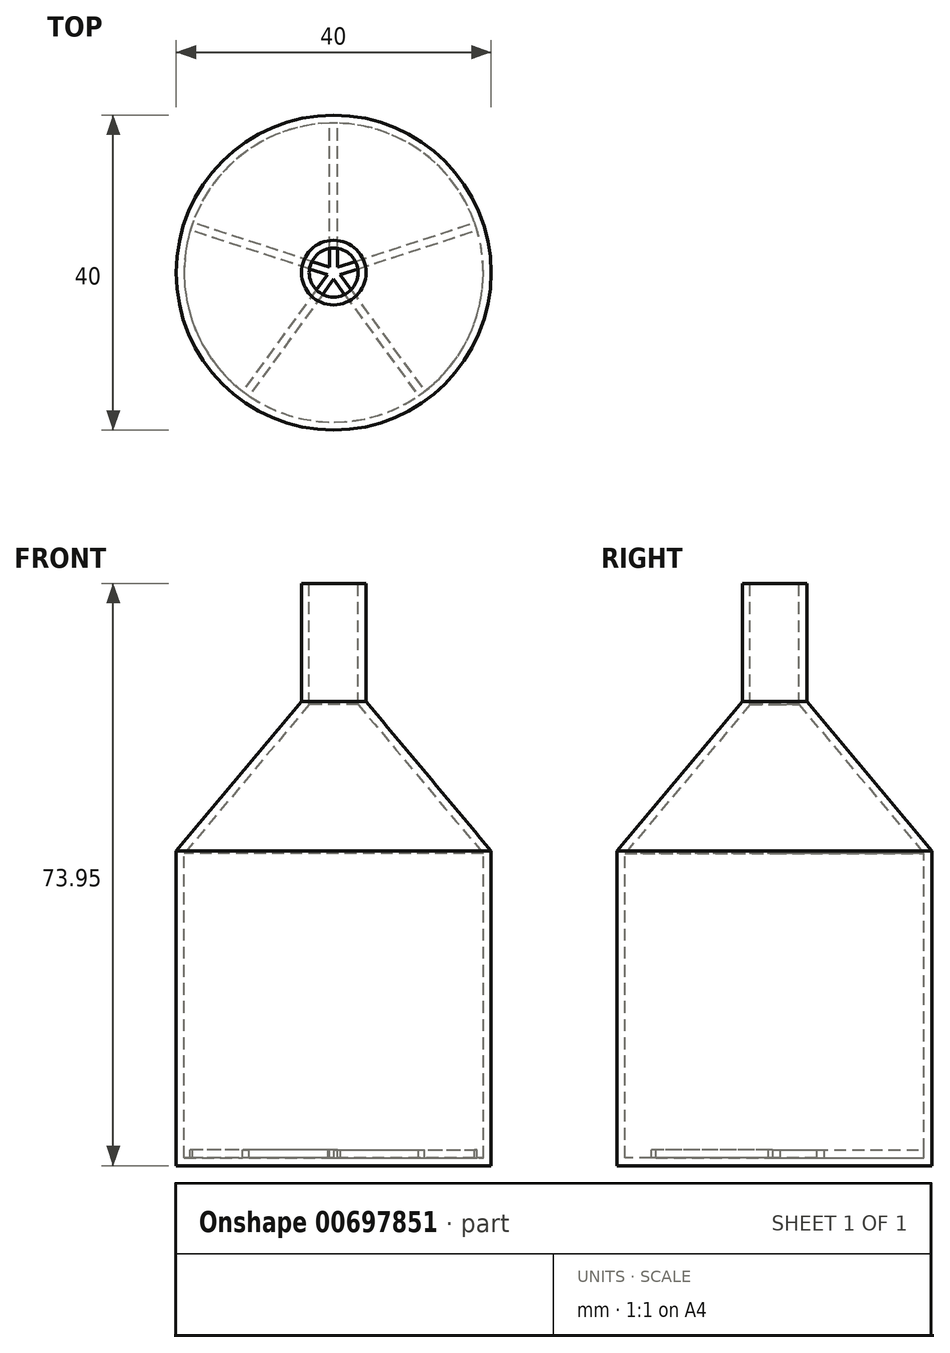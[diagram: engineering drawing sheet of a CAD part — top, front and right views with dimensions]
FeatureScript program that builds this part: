
annotation { "Feature Type Name" : "Feature", "Feature Type Description" : "" }
export const myFeature = defineFeature(function(context is Context, id is Id, definition is map)
    precondition{}
    {
        {
            var Q0;
            Q0=qCreatedBy(makeId("Front.planeOp"),FACE);
            var sketch = newSketch(context, id + "F0", { "sketchPlane" : qUnion([Q0])});
            skLineSegment(sketch, "E0", {"start": v(0, -1) * mm, "end": v(20, -1) * mm});
            skLineSegment(sketch, "E1", {"start": v(20, -1) * mm, "end": v(20, 39) * mm});
            skLineSegment(sketch, "E2", {"start": v(20, 39) * mm, "end": v(4.1, 57.95) * mm});
            skLineSegment(sketch, "E3", {"start": v(4.1, 57.95) * mm, "end": v(4.1, 72.95) * mm});
            skLineSegment(sketch, "E4", {"start": v(4.1, 72.95) * mm, "end": v(3.1, 72.95) * mm});
            skLineSegment(sketch, "E5.0", {"start": v(3.1, 57.58) * mm, "end": v(3.1, 72.95) * mm});
            skLineSegment(sketch, "E5.1", {"start": v(19, 38.64) * mm, "end": v(3.1, 57.58) * mm});
            skLineSegment(sketch, "E5.2", {"start": v(19, 0) * mm, "end": v(19, 38.64) * mm});
            skLineSegment(sketch, "E5.3", {"start": v(0, 0) * mm, "end": v(19, 0) * mm});
            skLineSegment(sketch, "E6", {"start": v(20, 39) * mm, "end": v(0, 39) * mm, "construction": true});
            skLineSegment(sketch, "E7", {"start": v(0, 0) * mm, "end": v(0, -1) * mm});
            skSolve(sketch);
        }
        {
            var Q0;
            Q0 = qSketchRegion(id + "F0", true);
            var Q1;
            Q1=sQuery(id+"F0.wireOp",EDGE,"E7");
            revolve(context, id + "F1", {"surfaceOperationType" : NewSurfaceOperationType.NEW, "entities" : qUnion([Q0]), "axis" : qUnion([Q1]), "revolveType" : RevolveType.FULL});
        }
        {
            var Q0;
            Q0=qCreatedBy(makeId("Top.planeOp"),FACE);
            var sketch = newSketch(context, id + "F2", { "sketchPlane" : qUnion([Q0])});
            skCircle(sketch, "E8.cCircle", {"center": v(0, 0) * mm, "radius": 16.18 * mm, "construction": true});
            skLineSegment(sketch, "E8.0", {"start": v(11.76, -16.18) * mm, "end": v(-11.76, -16.18) * mm, "construction": true});
            skLineSegment(sketch, "E8.1", {"start": v(-11.76, -16.18) * mm, "end": v(-19.02, 6.18) * mm, "construction": true});
            skLineSegment(sketch, "E8.2", {"start": v(-19.02, 6.18) * mm, "end": v(0, 20) * mm, "construction": true});
            skLineSegment(sketch, "E8.3", {"start": v(0, 20) * mm, "end": v(19.02, 6.18) * mm, "construction": true});
            skLineSegment(sketch, "E8.4", {"start": v(19.02, 6.18) * mm, "end": v(11.76, -16.18) * mm, "construction": true});
            skPoint(sketch, "E8.0.midPoint", {"position": v(0, -16.18) * mm});
            skArc(sketch, "E9.0", {"start": v(11.35, -16.47) * mm, "mid": v(11.76, -16.18) * mm, "end": v(12.16, -15.88) * mm});
            skLineSegment(sketch, "E10", {"start": v(0, 0) * mm, "end": v(-11.76, -16.18) * mm, "construction": true});
            skLineSegment(sketch, "E11", {"start": v(0, 0) * mm, "end": v(11.76, -16.18) * mm, "construction": true});
            skLineSegment(sketch, "E12", {"start": v(0, 0) * mm, "end": v(19.02, 6.18) * mm, "construction": true});
            skLineSegment(sketch, "E13", {"start": v(0, 0) * mm, "end": v(0, 20) * mm, "construction": true});
            skLineSegment(sketch, "E14", {"start": v(0, 0) * mm, "end": v(-19.02, 6.18) * mm, "construction": true});
            skLineSegment(sketch, "E15.0", {"start": v(-0.8, -0.26) * mm, "end": v(-12.16, -15.88) * mm});
            skLineSegment(sketch, "E16.0", {"start": v(0, -0.85) * mm, "end": v(-11.35, -16.47) * mm});
            skLineSegment(sketch, "E17.0", {"start": v(0.8, -0.26) * mm, "end": v(12.16, -15.88) * mm});
            skLineSegment(sketch, "E18.0", {"start": v(0, -0.85) * mm, "end": v(11.35, -16.47) * mm});
            skLineSegment(sketch, "E19.0", {"start": v(0.8, -0.26) * mm, "end": v(19.17, 5.7) * mm});
            skLineSegment(sketch, "E20.0", {"start": v(0.5, 0.69) * mm, "end": v(18.86, 6.65) * mm});
            skLineSegment(sketch, "E21.0", {"start": v(0.5, 0.69) * mm, "end": v(0.5, 20) * mm});
            skLineSegment(sketch, "E22.0", {"start": v(-0.5, 0.69) * mm, "end": v(-0.5, 20) * mm});
            skLineSegment(sketch, "E23.0", {"start": v(-0.8, -0.26) * mm, "end": v(-19.17, 5.7) * mm});
            skLineSegment(sketch, "E24.0", {"start": v(-0.5, 0.69) * mm, "end": v(-18.86, 6.65) * mm});
            skArc(sketch, "E25.trimOffspring", {"start": v(-12.16, -15.88) * mm, "mid": v(-11.76, -16.18) * mm, "end": v(-11.35, -16.47) * mm});
            skArc(sketch, "E26.trimOffspring", {"start": v(19.17, 5.7) * mm, "mid": v(19.02, 6.18) * mm, "end": v(18.86, 6.65) * mm});
            skArc(sketch, "E27.trimOffspring", {"start": v(0.5, 20) * mm, "mid": v(0, 20) * mm, "end": v(-0.5, 20) * mm});
            skArc(sketch, "E28.trimOffspring", {"start": v(-18.86, 6.65) * mm, "mid": v(-19.02, 6.18) * mm, "end": v(-19.17, 5.7) * mm});
            skSolve(sketch);
        }
        {
            var Q0;
            Q0 = qSketchRegion(id + "F2", true);
            extrude(context, id + "F3", {"entities" : qUnion([Q0]), "operationType" : NewBodyOperationType.ADD, "depth" : 1 * mm, "offsetDistance" : 25 * mm});
        }
    });
